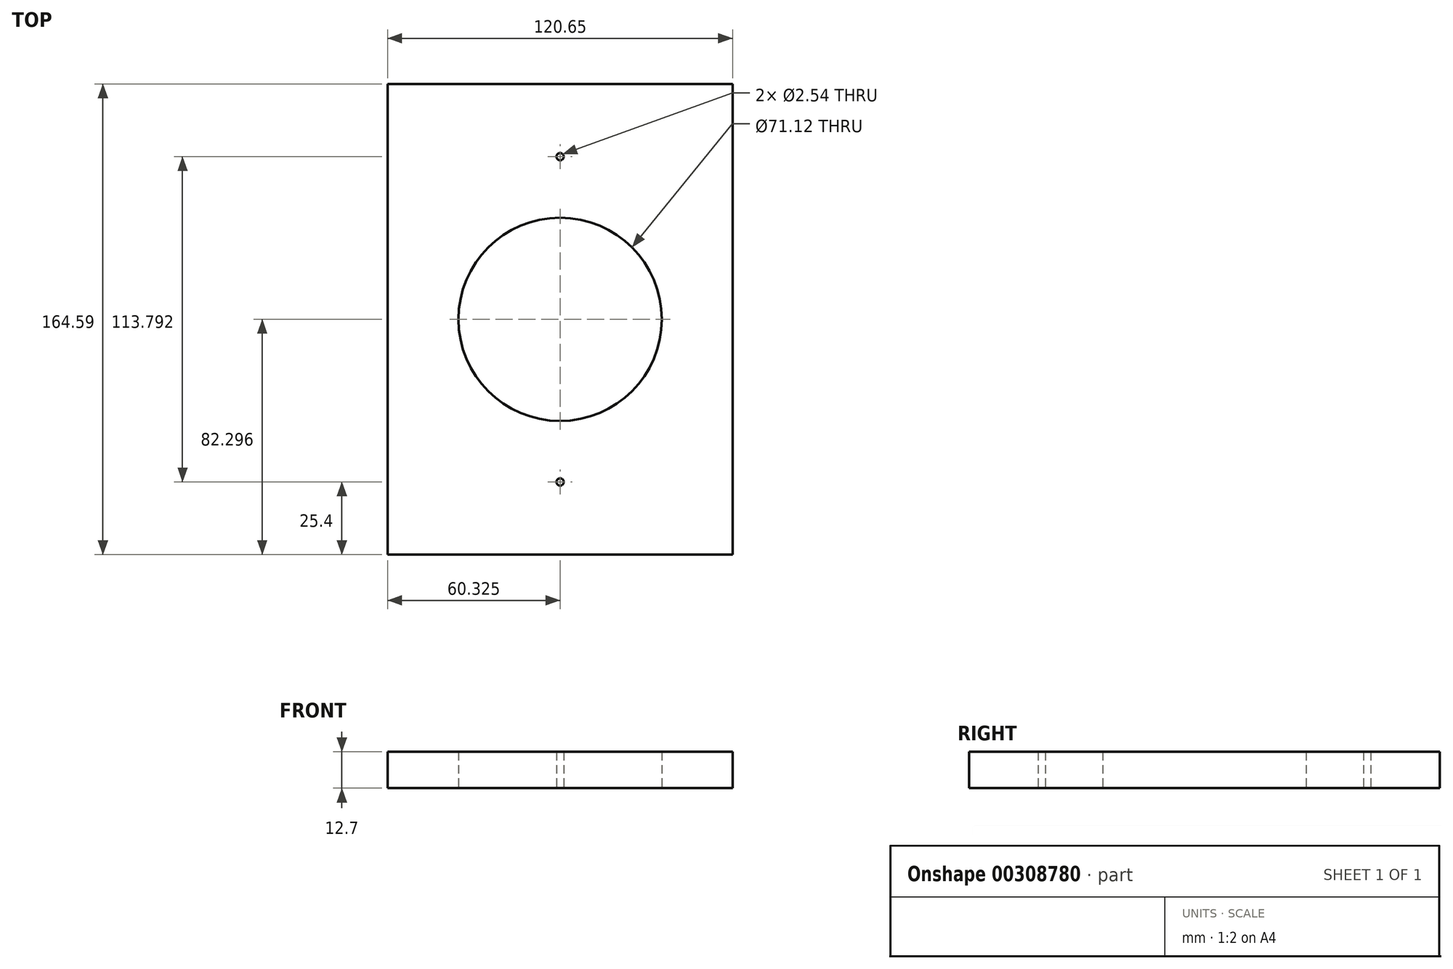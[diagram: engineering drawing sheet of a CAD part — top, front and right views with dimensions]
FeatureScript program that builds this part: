
annotation { "Feature Type Name" : "Feature", "Feature Type Description" : "" }
export const myFeature = defineFeature(function(context is Context, id is Id, definition is map)
    precondition{}
    {
        {
            var Q0;
            Q0=qCreatedBy(makeId("Top.planeOp"),FACE);
            var sketch = newSketch(context, id + "F0", { "sketchPlane" : qUnion([Q0])});
            skLineSegment(sketch, "E0.bottom", {"start": v(0, 0) * mm, "end": v(120.65, 0) * mm});
            skLineSegment(sketch, "E0.top", {"start": v(0, 164.6) * mm, "end": v(120.65, 164.6) * mm});
            skLineSegment(sketch, "E0.left", {"start": v(0, 0) * mm, "end": v(0, 164.6) * mm});
            skLineSegment(sketch, "E0.right", {"start": v(120.65, 0) * mm, "end": v(120.65, 164.6) * mm});
            skCircle(sketch, "E1", {"center": v(60.33, 25.4) * mm, "radius": 1.27 * mm});
            skCircle(sketch, "E2", {"center": v(60.32, 139.2) * mm, "radius": 1.27 * mm});
            skCircle(sketch, "E3", {"center": v(60.32, 82.3) * mm, "radius": 35.56 * mm});
            skSolve(sketch);
        }
        {
            var Q0;
            Q0=makeQuery(id+"F0.imprint","IMPRINT",FACE,{"disambiguationData":[TD([[makeQuery(id+"F0.imprint","IMPRINT",EDGE,{"derivedFrom":sQuery(id+"F0.wireOp",EDGE,"E0.bottom")}),1.0]])]});
            extrude(context, id + "F1", {"entities" : qUnion([Q0]), "depth" : 12.7 * mm});
        }
    });
